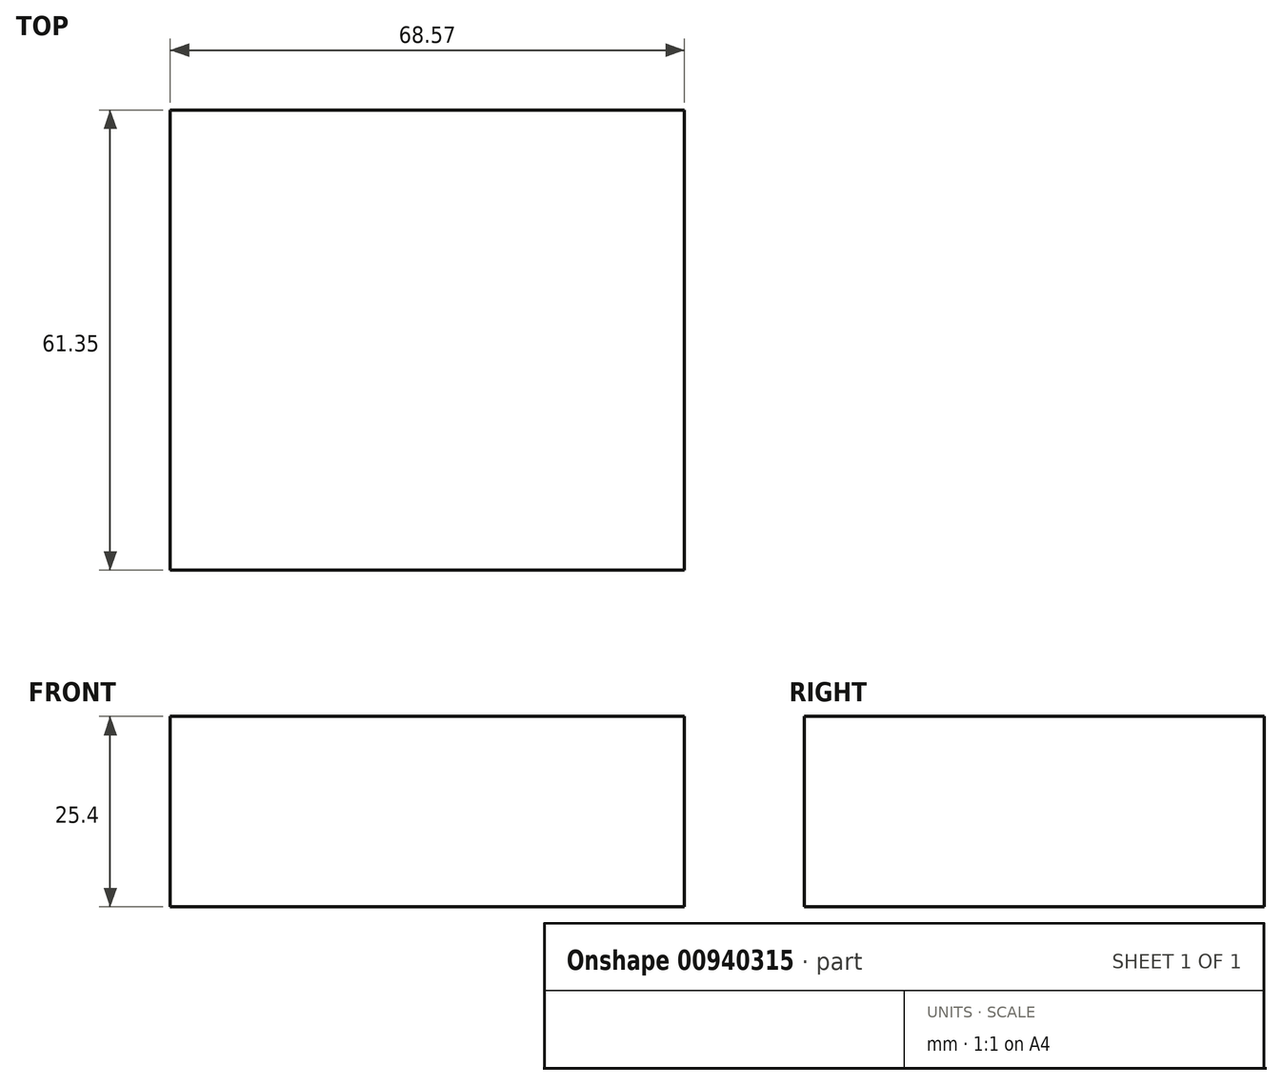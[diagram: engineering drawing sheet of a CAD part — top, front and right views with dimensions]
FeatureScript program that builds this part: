
annotation { "Feature Type Name" : "Feature", "Feature Type Description" : "" }
export const myFeature = defineFeature(function(context is Context, id is Id, definition is map)
    precondition{}
    {
        {
            var Q0;
            Q0=qCreatedBy(makeId("Top.planeOp"),FACE);
            var sketch = newSketch(context, id + "F0", { "sketchPlane" : qUnion([Q0])});
            skLineSegment(sketch, "E0.bottom", {"start": v(-31.77, 28.84) * mm, "end": v(36.8, 28.84) * mm});
            skLineSegment(sketch, "E0.top", {"start": v(-31.77, -32.5) * mm, "end": v(36.8, -32.5) * mm});
            skLineSegment(sketch, "E0.left", {"start": v(-31.77, 28.84) * mm, "end": v(-31.77, -32.5) * mm});
            skLineSegment(sketch, "E0.right", {"start": v(36.8, 28.84) * mm, "end": v(36.8, -32.5) * mm});
            skSolve(sketch);
        }
        {
            var Q0;
            Q0=makeQuery(id+"F0.imprint","IMPRINT",FACE,{"disambiguationData":[TD([[makeQuery(id+"F0.imprint","IMPRINT",EDGE,{"derivedFrom":sQuery(id+"F0.wireOp",EDGE,"E0.bottom")}),-1.0]])]});
            extrude(context, id + "F1", {"entities" : qUnion([Q0]), "depth" : 25.4 * mm, "offsetDistance" : 25.4 * mm});
        }
    });
